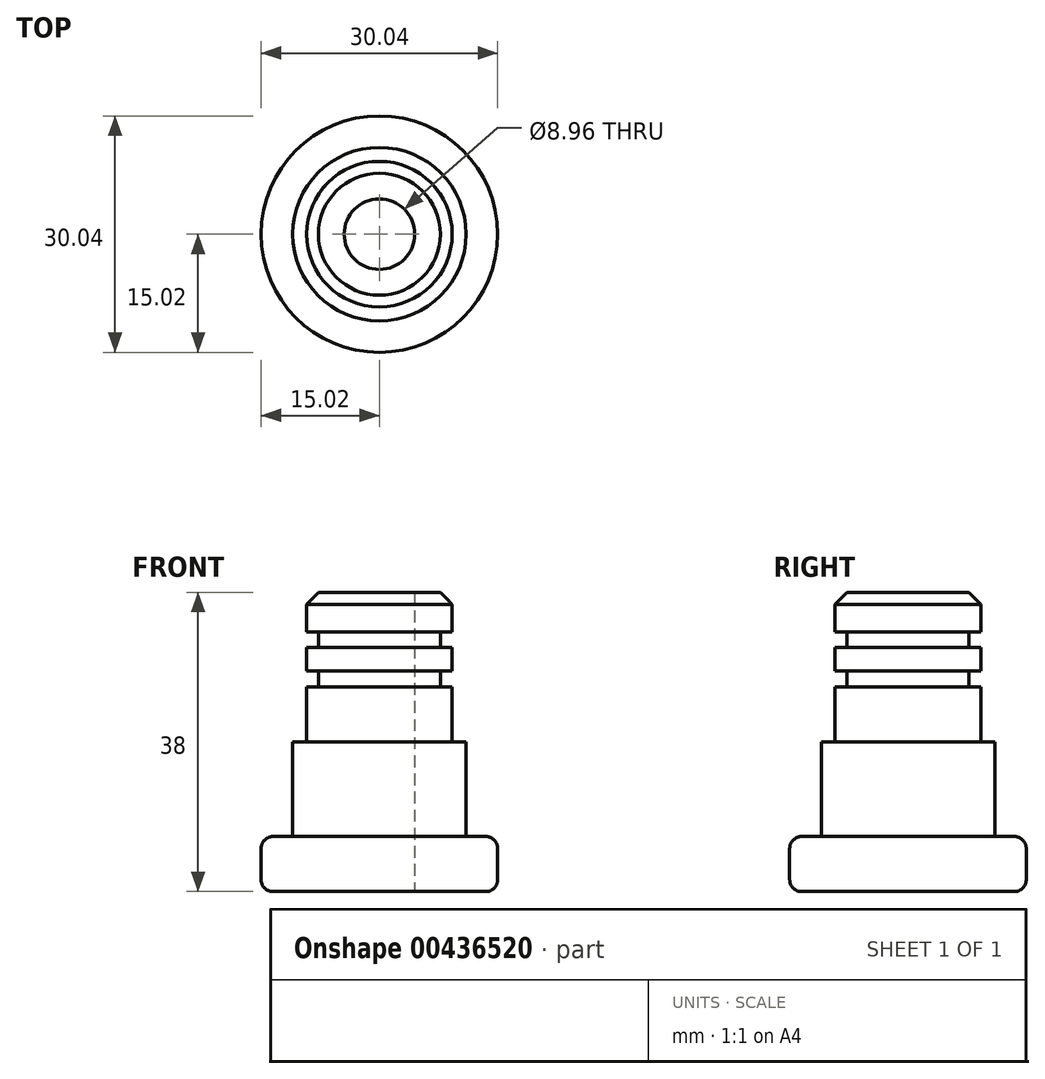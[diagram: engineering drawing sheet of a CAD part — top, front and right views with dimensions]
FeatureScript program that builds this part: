
annotation { "Feature Type Name" : "Feature", "Feature Type Description" : "" }
export const myFeature = defineFeature(function(context is Context, id is Id, definition is map)
    precondition{}
    {
        {
            var Q0;
            Q0=qCreatedBy(makeId("Top.planeOp"),FACE);
            var sketch = newSketch(context, id + "F0", { "sketchPlane" : qUnion([Q0])});
            skCircle(sketch, "E0", {"center": v(0, 0) * mm, "radius": 15.02 * mm});
            skSolve(sketch);
        }
        {
            var Q0;
            Q0 = qSketchRegion(id + "F0", true);
            extrude(context, id + "F1", {"entities" : qUnion([Q0]), "depth" : 7 * mm});
        }
        {
            var Q0;
            Q0=makeQuery(id+"F1.opExtrude","CAP_FACE",FACE,{"disambiguationData":[OSD([sQuery(id+"F0.wireOp",EDGE,"E0")])],"isStart":false});
            var sketch = newSketch(context, id + "F2", { "sketchPlane" : qUnion([Q0])});
            skCircle(sketch, "E1", {"center": v(0, 0) * mm, "radius": 11.02 * mm});
            skSolve(sketch);
        }
        {
            var Q0;
            Q0 = qSketchRegion(id + "F2", true);
            extrude(context, id + "F3", {"entities" : qUnion([Q0]), "operationType" : NewBodyOperationType.ADD, "depth" : 12 * mm});
        }
        {
            var Q0;
            Q0=makeQuery(id+"F3.opExtrude","CAP_FACE",FACE,{"disambiguationData":[OSD([sQuery(id+"F2.wireOp",EDGE,"E1")])],"isStart":false});
            var sketch = newSketch(context, id + "F4", { "sketchPlane" : qUnion([Q0])});
            skCircle(sketch, "E2", {"center": v(0, 0) * mm, "radius": 9.25 * mm});
            skSolve(sketch);
        }
        {
            var Q0;
            Q0 = qSketchRegion(id + "F4", true);
            extrude(context, id + "F5", {"entities" : qUnion([Q0]), "operationType" : NewBodyOperationType.ADD, "depth" : 7 * mm});
        }
        {
            var Q0;
            Q0=makeQuery(id+"F5.opExtrude","CAP_FACE",FACE,{"disambiguationData":[OSD([sQuery(id+"F4.wireOp",EDGE,"E2")])],"isStart":false});
            var sketch = newSketch(context, id + "F6", { "sketchPlane" : qUnion([Q0])});
            skCircle(sketch, "E3", {"center": v(0, 0) * mm, "radius": 7.75 * mm});
            skSolve(sketch);
        }
        {
            var Q0;
            Q0 = qSketchRegion(id + "F6", true);
            extrude(context, id + "F7", {"entities" : qUnion([Q0]), "operationType" : NewBodyOperationType.ADD, "depth" : 2 * mm});
        }
        {
            var Q0;
            Q0=makeQuery(id+"F7.opExtrude","CAP_FACE",FACE,{"disambiguationData":[OSD([sQuery(id+"F6.wireOp",EDGE,"E3")])],"isStart":false});
            var sketch = newSketch(context, id + "F8", { "sketchPlane" : qUnion([Q0])});
            skCircle(sketch, "E4", {"center": v(0, 0) * mm, "radius": 9.24 * mm});
            skSolve(sketch);
        }
        {
            var Q0;
            Q0 = qSketchRegion(id + "F8", true);
            extrude(context, id + "F9", {"entities" : qUnion([Q0]), "operationType" : NewBodyOperationType.ADD, "depth" : 3 * mm});
        }
        {
            var Q0;
            Q0=makeQuery(id+"F9.opExtrude","CAP_FACE",FACE,{"disambiguationData":[OSD([sQuery(id+"F8.wireOp",EDGE,"E4")])],"isStart":false});
            var sketch = newSketch(context, id + "F10", { "sketchPlane" : qUnion([Q0])});
            skCircle(sketch, "E5", {"center": v(0, 0) * mm, "radius": 7.74 * mm});
            skSolve(sketch);
        }
        {
            var Q0;
            Q0 = qSketchRegion(id + "F10", true);
            extrude(context, id + "F11", {"entities" : qUnion([Q0]), "operationType" : NewBodyOperationType.ADD, "depth" : 2 * mm});
        }
        {
            var Q0;
            Q0=makeQuery(id+"F11.opExtrude","CAP_FACE",FACE,{"disambiguationData":[OSD([sQuery(id+"F10.wireOp",EDGE,"E5")])],"isStart":false});
            var sketch = newSketch(context, id + "F12", { "sketchPlane" : qUnion([Q0])});
            skCircle(sketch, "E6", {"center": v(0, 0) * mm, "radius": 9.25 * mm});
            skSolve(sketch);
        }
        {
            var Q0;
            Q0 = qSketchRegion(id + "F12", true);
            extrude(context, id + "F13", {"entities" : qUnion([Q0]), "operationType" : NewBodyOperationType.ADD, "depth" : 5 * mm});
        }
        {
            var Q0;
            Q0=makeQuery(id+"F13.opExtrude","CAP_EDGE",EDGE,{"disambiguationData":[OSD([sQuery(id+"F12.wireOp",EDGE,"E6")])],"isStart":false});
            chamfer(context, id + "F14", {"entities" : qUnion([Q0]), "width" : 1.5 * mm, "tangentPropagation" : true});
        }
        {
            var Q0;
            Q0=makeQuery(id+"F1.opExtrude","CAP_EDGE",EDGE,{"disambiguationData":[OSD([sQuery(id+"F0.wireOp",EDGE,"E0")])],"isStart":false});
            var Q1;
            Q1=makeQuery(id+"F1.opExtrude","CAP_EDGE",EDGE,{"disambiguationData":[OSD([sQuery(id+"F0.wireOp",EDGE,"E0")])],"isStart":true});
            fillet(context, id + "F15", {"entities" : qUnion([Q0, Q1]), "radius" : 1.5 * mm, "tangentPropagation" : true, "allowEdgeOverflow" : false});
        }
        {
            var Q0;
            Q0=qCreatedBy(makeId("Top.planeOp"),FACE);
            var sketch = newSketch(context, id + "F16", { "sketchPlane" : qUnion([Q0])});
            skCircle(sketch, "E7", {"center": v(0, 0) * mm, "radius": 4.48 * mm});
            skSolve(sketch);
        }
        {
            var Q0;
            Q0 = qSketchRegion(id + "F16", true);
            extrude(context, id + "F17", {"entities" : qUnion([Q0]), "operationType" : NewBodyOperationType.REMOVE, "depth" : 50 * mm});
        }
    });
